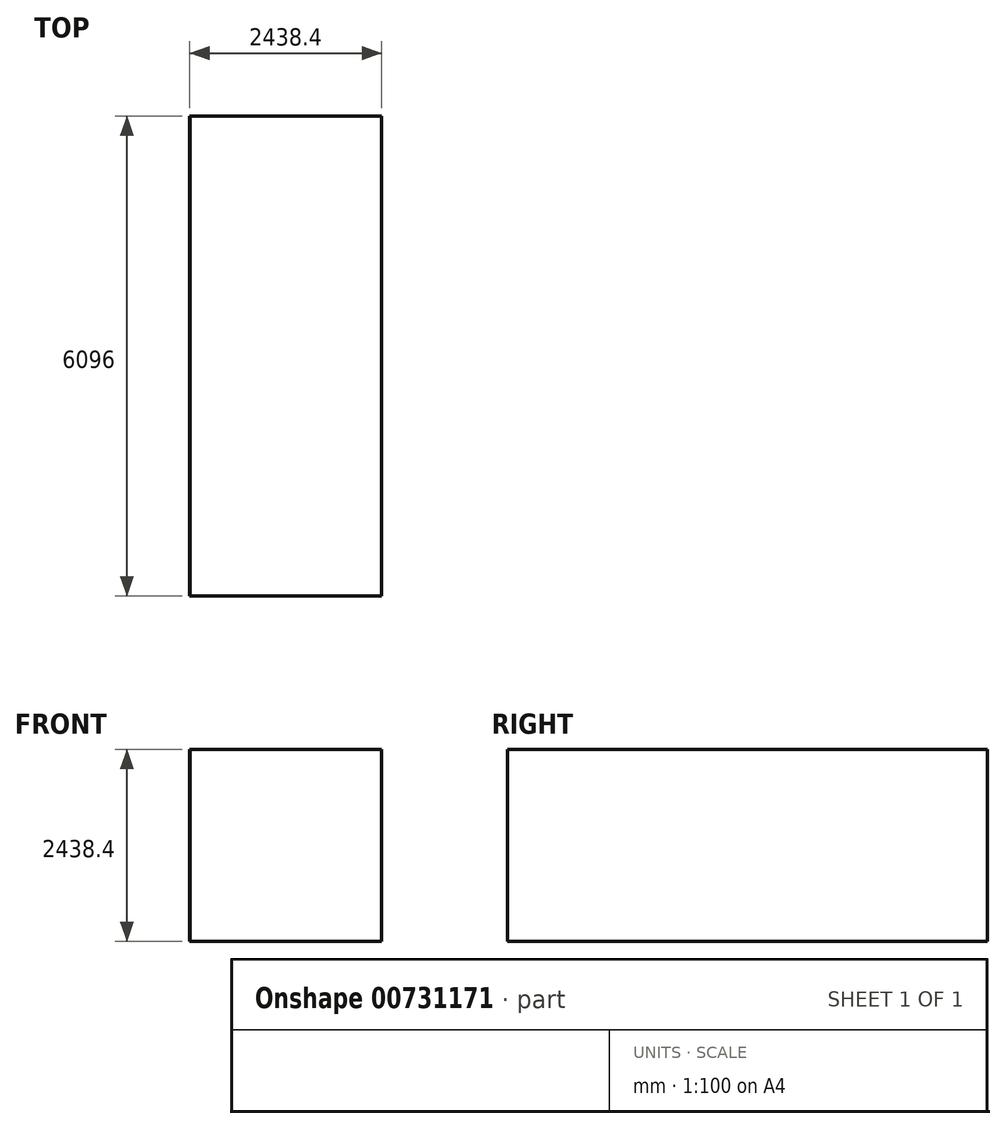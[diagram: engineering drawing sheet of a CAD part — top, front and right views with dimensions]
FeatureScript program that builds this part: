
annotation { "Feature Type Name" : "Feature", "Feature Type Description" : "" }
export const myFeature = defineFeature(function(context is Context, id is Id, definition is map)
    precondition{}
    {
        {
            var Q0;
            Q0=qCreatedBy(makeId("Top.planeOp"),FACE);
            var sketch = newSketch(context, id + "F0", { "sketchPlane" : qUnion([Q0])});
            skLineSegment(sketch, "E0.bottom", {"start": v(-1219.2, 3048) * mm, "end": v(1219.2, 3048) * mm});
            skLineSegment(sketch, "E0.top", {"start": v(-1219.2, -3048) * mm, "end": v(1219.2, -3048) * mm});
            skLineSegment(sketch, "E0.left", {"start": v(-1219.2, 3048) * mm, "end": v(-1219.2, -3048) * mm});
            skLineSegment(sketch, "E0.right", {"start": v(1219.2, 3048) * mm, "end": v(1219.2, -3048) * mm});
            skPoint(sketch, "E0.middle", {"position": v(0, 0) * mm});
            skSolve(sketch);
        }
        {
            var Q0;
            Q0 = qSketchRegion(id + "F0", true);
            extrude(context, id + "F1", {"entities" : qUnion([Q0]), "depth" : 2438.4 * mm, "offsetDistance" : 25.4 * mm});
        }
        {
            var Q0;
            Q0=makeQuery(id+"F1.opExtrude","CAP_FACE",FACE,{"disambiguationData":[OSD([sQuery(id+"F0.wireOp",EDGE,"E0.bottom"),sQuery(id+"F0.wireOp",EDGE,"E0.top"),sQuery(id+"F0.wireOp",EDGE,"E0.left"),sQuery(id+"F0.wireOp",EDGE,"E0.right")])],"isStart":false});
            var Q1;
            Q1=makeQuery(id+"F1.opExtrude","SWEPT_FACE",FACE,{"disambiguationData":[OSD([sQuery(id+"F0.wireOp",EDGE,"E0.top")])]});
            shell(context, id + "F2", {"entities" : qUnion([Q0, Q1]), "thickness" : 2.54 * mm});
        }
    });
